# Revit family: TLI - Royal TEB - Wall
name_source: partatom
category: Lighting Fixtures
revit_build: Autodesk Revit 2014 (Build: 20130709_2115(x64)
units: mm (PartAtom-declared; Revit-internal decimal feet)

## types (16) — shared parameters
ADA Compliant = No
Amps = 1
Color Filter = 16777215
Conditions of Use = Elements are representations. Color and detail may differ from actual product. Information is for general use and should be reviewed by a Professional.
Depth = 0' - 6"
Description = Architectectural Outdoor
Diffuser = Luminous White Acrylic
Diffuser Material = Acrylic - TLI - Luminous White
Dimming Lamp Color Temperature Shift = <None>
Distributor Locations = USA, Canada, Puerto Rico
Finish = Textured Black
Fixture = Steel
Fixture Material = Paint - TLI - Textured Black
Industry Standards = ETL
Integral Battery = No
Lamp Base = 4-Pin
Length = 1' - 1 1/2"
Manufacturer = Teron Lighting
Manufacturer Telephone = 01-513-858-6004
MasterFormat 2004 Number = 26.56.00
MasterFormat 2004 Title = Exterior Lighting
Mounting Type = 4" Junction Box
Photometric Web File = generic.ies
Point of Final Manufacture = Fairfield, OH, USA
Product = Royal TEB
Product Documentation URL = http://teronlighting.com
Product Page URL = http://teronlighting.com
Remote Battery = No
Requires Special Disposal = No
Tilt Angle = 0.00°
URL = http://teronlighting.com
Width = 0' - 8 1/4"
zero-valued in all types: Cost, Percentage Post-Consumer, Percentage Pre-Consumer

## per-type parameters (varying)
| type | Apparent Load | Lamp | Model | Number of Lamps | Voltage | Watts |
| QE 1 -  13W - 120V | 13 VA | 1 - 13W QE | RL - F113Q-TEB | 1 | 120 V | 13 W |
| QE 1 -  13W - 277V | 13 VA | 1 - 13W QE | RL - F113Q-TEB | 1 | 277 V | 13 W |
| QE 2 -  13W - 120V | 26 VA | 2 - 18W QE | RL - F213Q-TEB | 2 | 120 V | 26 W |
| QE 2 -  13W - 277V | 26 VA | 2 - 18W QE | RL - F213Q-TEB | 2 | 277 V | 26 W |
| QE 1 -  18W - 120V | 18 VA | 1 - 18W QE | RL - F118Q-TEB | 1 | 120 V | 18 W |
| QE 1 -  18W - 277V | 18 VA | 1 - 18W QE | RL - F118Q-TEB | 1 | 277 V | 18 W |
| QE 2 -  18W - 120V | 36 VA | 2 - 18W QE | RL - F218Q-TEB | 2 | 120 V | 36 W |
| QE 2 -  18W - 277V | 36 VA | 2 - 18W QE | RL - F218Q-TEB | 2 | 277 V | 36 W |
| QE 1 -  26W - 120V | 26 VA | 1 - 26W QE | RL - F126Q -TEB | 1 | 120 V | 26 W |
| QE 1 -  26W - 277V | 26 VA | 1 - 26W QE | RL - F126Q -TEB | 1 | 277 V | 26 W |
| QE 2 -  26W - 120V | 52 VA | 2 - 26W TBX | RL - F226Q -TEB | 2 | 120 V | 52 W |
| QE 2 -  26W - 277V | 52 VA | 2 - 26W TBX | RL - F226Q-TEB | 2 | 277 V | 52 W |
| TBX 1 -  32W - 120V | 32 VA | 1 - 32W  TBX | RL - F132X-TEB | 1 | 120 V | 32 W |
| TBX 1 -  32W - 277V | 32 VA | 1 - 32W  TBX | RL - F132X-TEB | 1 | 277 V | 32 W |
| TBX 1 -  42W - 120V | 42 VA | 1 - 42W TBX | RL - F142X-TEB | 1 | 120 V | 42 W |
| TBX 1 -  42W - 277V | 42 VA | 1 - 42W TBX | RL - F142X-TEB | 1 | 277 V | 42 W |

## geometry (parser evidence)
native form markers: Blend x10, Sweep x4
no freeform markers — native parametric forms only
